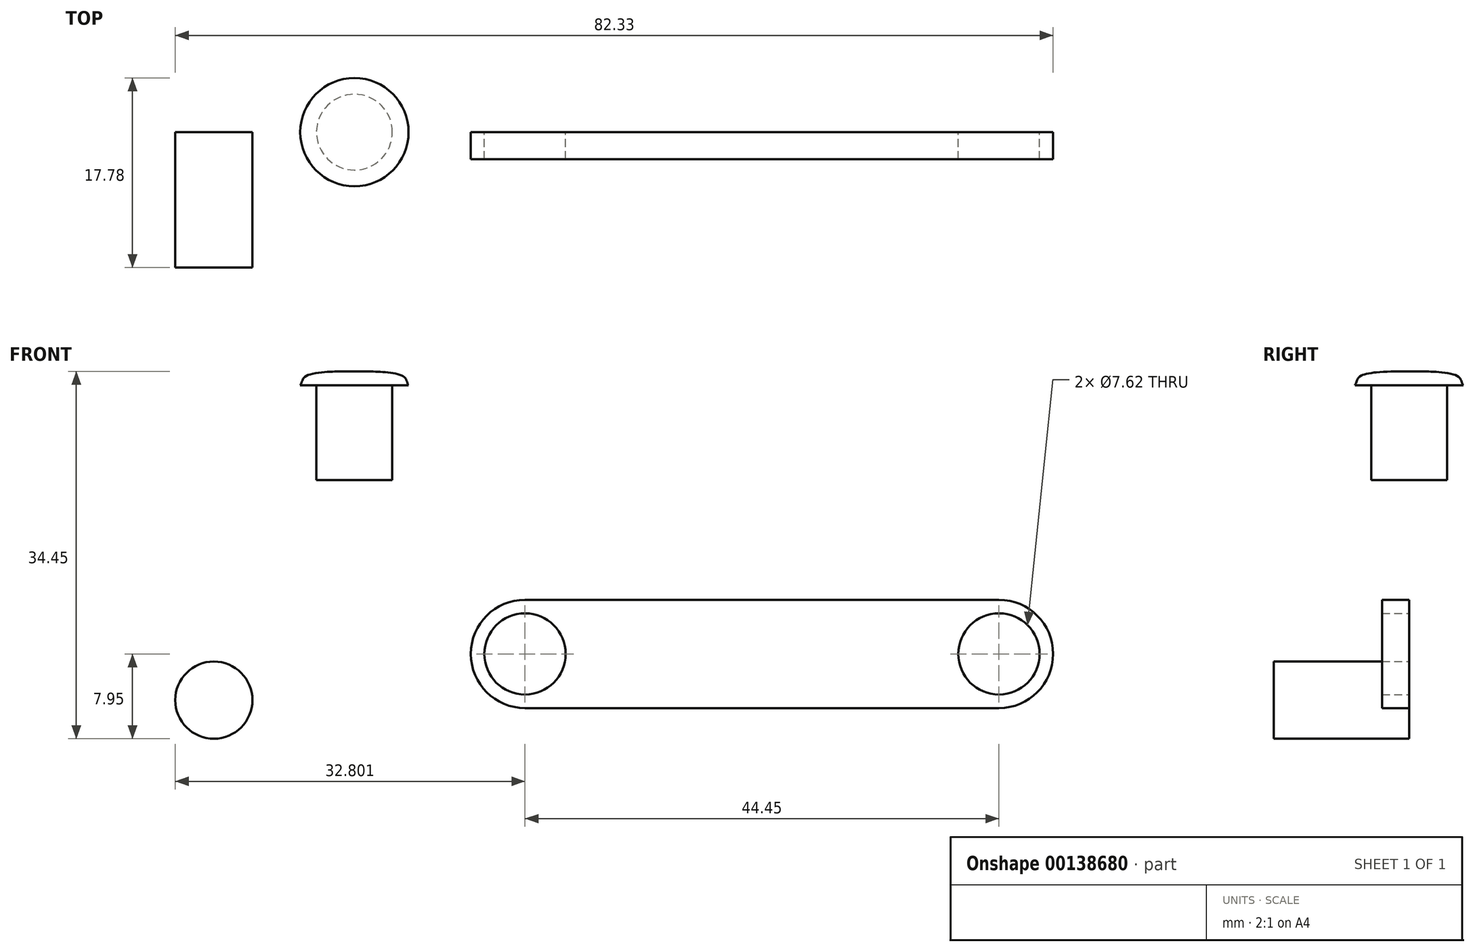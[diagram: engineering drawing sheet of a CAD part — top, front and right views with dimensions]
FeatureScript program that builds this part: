
annotation { "Feature Type Name" : "Feature", "Feature Type Description" : "" }
export const myFeature = defineFeature(function(context is Context, id is Id, definition is map)
    precondition{}
    {
        {
            var Q0;
            Q0=qCreatedBy(makeId("Front.planeOp"),FACE);
            var sketch = newSketch(context, id + "F0", { "sketchPlane" : qUnion([Q0])});
            skCircle(sketch, "E0", {"center": v(-983.12, 469.89) * mm, "radius": 3.62 * mm});
            skLineSegment(sketch, "E1.bottom", {"start": v(-959.02, 479.3) * mm, "end": v(-904.4, 479.3) * mm});
            skLineSegment(sketch, "E1.top", {"start": v(-959.02, 469.14) * mm, "end": v(-904.4, 469.14) * mm});
            skLineSegment(sketch, "E1.left", {"start": v(-959.02, 479.3) * mm, "end": v(-959.02, 469.14) * mm});
            skLineSegment(sketch, "E1.right", {"start": v(-904.4, 479.3) * mm, "end": v(-904.4, 469.14) * mm});
            skCircle(sketch, "E2", {"center": v(-953.94, 474.22) * mm, "radius": 3.81 * mm});
            skCircle(sketch, "E3", {"center": v(-909.49, 474.22) * mm, "radius": 3.81 * mm});
            skCircle(sketch, "E4", {"center": v(-909.49, 474.22) * mm, "radius": 5.08 * mm});
            skCircle(sketch, "E5", {"center": v(-953.94, 474.22) * mm, "radius": 5.08 * mm});
            skSolve(sketch);
        }
        {
            var Q0;
            Q0=makeQuery(id+"F0.imprint","IMPRINT",FACE,{"disambiguationData":[TD([[makeQuery(id+"F0.imprint","IMPRINT",EDGE,{"derivedFrom":sQuery(id+"F0.wireOp",EDGE,"E0")}),1.0]])]});
            extrude(context, id + "F1", {"entities" : qUnion([Q0]), "depth" : 12.7 * mm});
        }
        {
            var Q0;
            Q0=makeQuery(id+"F0.imprint","IMPRINT",FACE,{"disambiguationData":[TD([[makeQuery(id+"F0.imprint","IMPRINT",EDGE,{"derivedFrom":sQuery(id+"F0.wireOp",EDGE,"E2")}),-1.0]])]});
            var Q1;
            Q1=makeQuery(id+"F0.imprint","IMPRINT",FACE,{"disambiguationData":[TD([[makeQuery(id+"F0.imprint","IMPRINT",EDGE,{"derivedFrom":sQuery(id+"F0.wireOp",EDGE,"E3")}),-1.0]])]});
            var Q2;
            {var subQ0=sQuery(id+"F0.wireOp",EDGE,"E5");var subQ1=sQuery(id+"F0.wireOp",EDGE,"E1.bottom");var subQ2=makeQuery(id+"F0.imprint","INTERSECT",VERTEX,{"derivedFrom":[subQ1,subQ0]});Q2=makeQuery(id+"F0.imprint","IMPRINT",FACE,{"disambiguationData":[TD([[makeQuery(id+"F0.imprint","IMPRINT",EDGE,{"disambiguationData":[TD([[subQ2,-1.0]])],"derivedFrom":subQ1}),-1.0]])]});}
            extrude(context, id + "F2", {"entities" : qUnion([Q0, Q1, Q2]), "depth" : 2.54 * mm});
        }
        {
            var Q0;
            Q0=qCreatedBy(makeId("Front.planeOp"),FACE);
            var sketch = newSketch(context, id + "F3", { "sketchPlane" : qUnion([Q0])});
            skLineSegment(sketch, "E6.bottom", {"start": v(-969.94, 499.42) * mm, "end": v(-966.38, 499.42) * mm});
            skLineSegment(sketch, "E6.top", {"start": v(-969.94, 490.53) * mm, "end": v(-966.38, 490.53) * mm});
            skLineSegment(sketch, "E6.left", {"start": v(-969.94, 499.42) * mm, "end": v(-969.94, 490.53) * mm});
            skLineSegment(sketch, "E6.right", {"start": v(-966.38, 499.42) * mm, "end": v(-966.38, 490.53) * mm});
            skLineSegment(sketch, "E7", {"start": v(-966.38, 499.42) * mm, "end": v(-964.86, 499.42) * mm});
            skLineSegment(sketch, "E8", {"start": v(-969.94, 499.42) * mm, "end": v(-969.94, 500.69) * mm});
            skFitSpline(sketch, "E9", {"points": [v(-969.94, 500.69) * mm, v(-967.49, 500.69) * mm, v(-965.23, 500.16) * mm, v(-964.86, 499.42) * mm], "startDerivative": vector(6.24, 0.24) * mm, "endDerivative": vector(2.28, -3.15) * mm});
            skSolve(sketch);
        }
        {
            var Q0;
            Q0=makeQuery(id+"F3.imprint","IMPRINT",FACE,{"disambiguationData":[TD([[makeQuery(id+"F3.imprint","IMPRINT",EDGE,{"derivedFrom":sQuery(id+"F3.wireOp",EDGE,"E6.bottom")}),-1.0]])]});
            var Q1;
            Q1=makeQuery(id+"F3.imprint","IMPRINT",FACE,{"disambiguationData":[TD([[makeQuery(id+"F3.imprint","IMPRINT",EDGE,{"derivedFrom":sQuery(id+"F3.wireOp",EDGE,"E6.bottom")}),1.0]])]});
            var Q2;
            Q2=sQuery(id+"F3.wireOp",EDGE,"E8");
            revolve(context, id + "F4", {"entities" : qUnion([Q0, Q1]), "axis" : qUnion([Q2]), "revolveType" : RevolveType.FULL});
        }
    });
